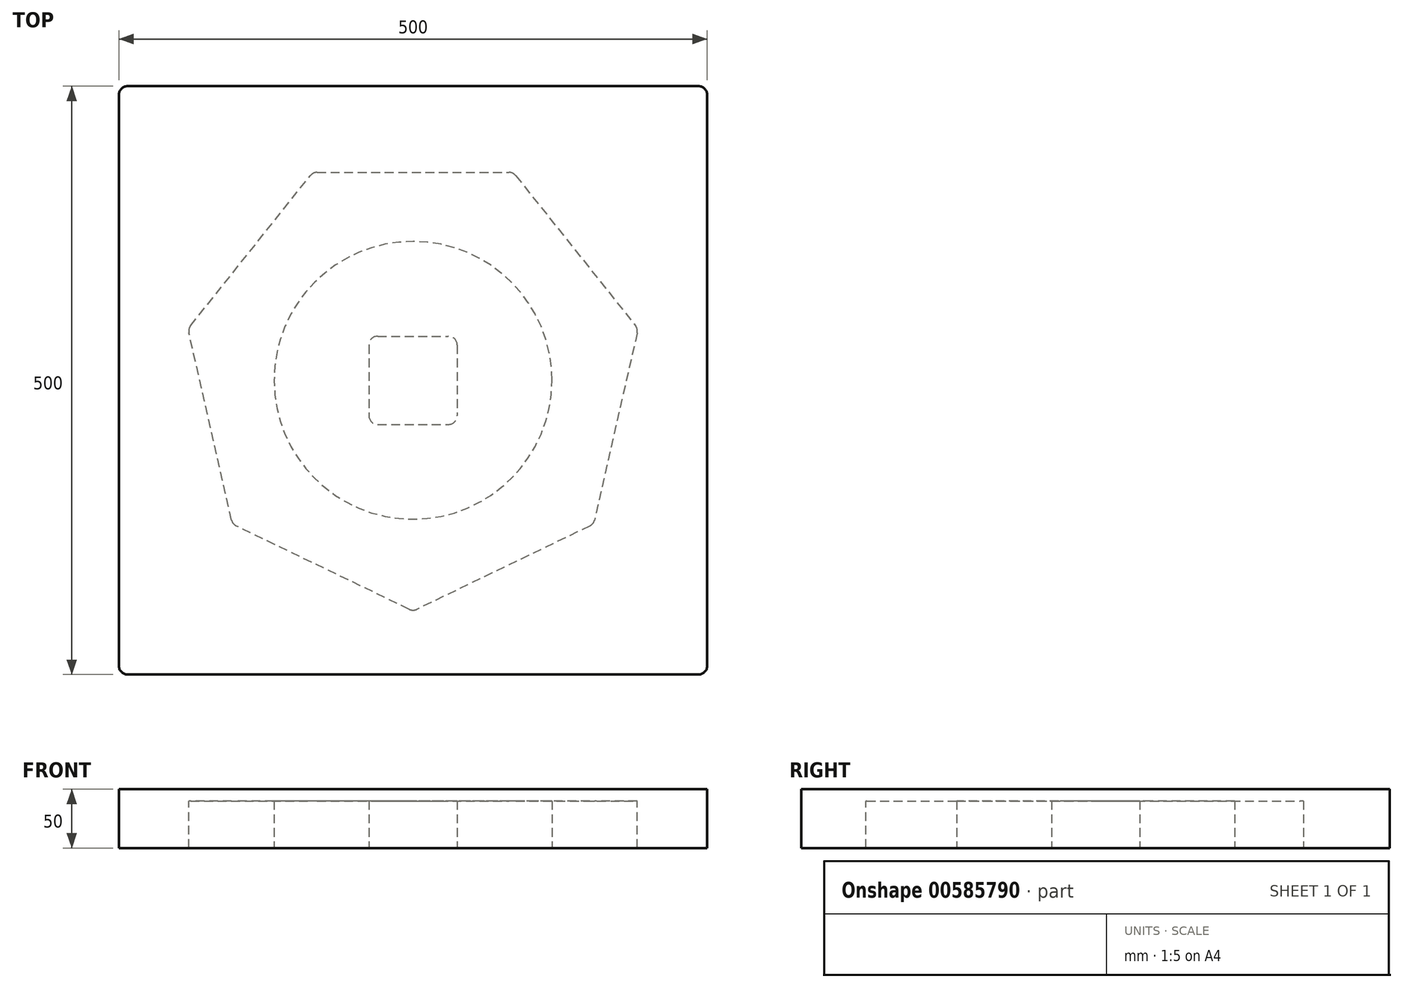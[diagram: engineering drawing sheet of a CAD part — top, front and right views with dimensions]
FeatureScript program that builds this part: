
annotation { "Feature Type Name" : "Feature", "Feature Type Description" : "" }
export const myFeature = defineFeature(function(context is Context, id is Id, definition is map)
    precondition{}
    {
        {
            var Q0;
            Q0=qCreatedBy(makeId("Top.planeOp"),FACE);
            var sketch = newSketch(context, id + "F0", { "sketchPlane" : qUnion([Q0])});
            skLineSegment(sketch, "E0.bottom", {"start": v(-250, 250) * mm, "end": v(250, 250) * mm});
            skLineSegment(sketch, "E0.top", {"start": v(-250, -250) * mm, "end": v(250, -250) * mm});
            skLineSegment(sketch, "E0.left", {"start": v(-250, 250) * mm, "end": v(-250, -250) * mm});
            skLineSegment(sketch, "E0.right", {"start": v(250, 250) * mm, "end": v(250, -250) * mm});
            skPoint(sketch, "E0.middle", {"position": v(0, 0) * mm});
            skCircle(sketch, "E1.cCircle", {"center": v(0, 0) * mm, "radius": 176.72 * mm, "construction": true});
            skLineSegment(sketch, "E1.0", {"start": v(-85.1, 176.72) * mm, "end": v(85.1, 176.72) * mm});
            skLineSegment(sketch, "E1.1", {"start": v(85.1, 176.72) * mm, "end": v(191.23, 43.65) * mm});
            skLineSegment(sketch, "E1.2", {"start": v(191.23, 43.65) * mm, "end": v(153.36, -122.3) * mm});
            skLineSegment(sketch, "E1.3", {"start": v(153.36, -122.3) * mm, "end": v(0, -196.15) * mm});
            skLineSegment(sketch, "E1.4", {"start": v(0, -196.15) * mm, "end": v(-153.36, -122.3) * mm});
            skLineSegment(sketch, "E1.5", {"start": v(-153.36, -122.3) * mm, "end": v(-191.23, 43.65) * mm});
            skLineSegment(sketch, "E1.6", {"start": v(-191.23, 43.65) * mm, "end": v(-85.1, 176.72) * mm});
            skPoint(sketch, "E1.0.midPoint", {"position": v(0, 176.72) * mm});
            skCircle(sketch, "E2", {"center": v(0, 0) * mm, "radius": 118.02 * mm});
            skLineSegment(sketch, "E3.bottom", {"start": v(-37.5, 37.5) * mm, "end": v(37.5, 37.5) * mm});
            skLineSegment(sketch, "E3.top", {"start": v(-37.5, -37.5) * mm, "end": v(37.5, -37.5) * mm});
            skLineSegment(sketch, "E3.left", {"start": v(-37.5, 37.5) * mm, "end": v(-37.5, -37.5) * mm});
            skLineSegment(sketch, "E3.right", {"start": v(37.5, 37.5) * mm, "end": v(37.5, -37.5) * mm});
            skSolve(sketch);
        }
        {
            var Q0;
            Q0=makeQuery(id+"F0.imprint","IMPRINT",FACE,{"disambiguationData":[TD([[makeQuery(id+"F0.imprint","IMPRINT",EDGE,{"derivedFrom":sQuery(id+"F0.wireOp",EDGE,"E0.bottom")}),-1.0]])]});
            var Q1;
            Q1=makeQuery(id+"F0.imprint","IMPRINT",FACE,{"disambiguationData":[TD([[makeQuery(id+"F0.imprint","IMPRINT",EDGE,{"derivedFrom":sQuery(id+"F0.wireOp",EDGE,"E2")}),1.0]])]});
            var Q2;
            Q2=makeQuery(id+"F0.imprint","IMPRINT",FACE,{"disambiguationData":[TD([[makeQuery(id+"F0.imprint","IMPRINT",EDGE,{"derivedFrom":sQuery(id+"F0.wireOp",EDGE,"E1.0")}),-1.0]])]});
            var Q3;
            Q3=makeQuery(id+"F0.imprint","IMPRINT",FACE,{"disambiguationData":[TD([[makeQuery(id+"F0.imprint","IMPRINT",EDGE,{"derivedFrom":sQuery(id+"F0.wireOp",EDGE,"E3.bottom")}),-1.0]])]});
            extrude(context, id + "F1", {"entities" : qUnion([Q0, Q1, Q2, Q3]), "depth" : 50 * mm, "offsetDistance" : 25 * mm});
        }
        {
            var Q0;
            Q0=makeQuery(id+"F0.imprint","IMPRINT",FACE,{"disambiguationData":[TD([[makeQuery(id+"F0.imprint","IMPRINT",EDGE,{"derivedFrom":sQuery(id+"F0.wireOp",EDGE,"E1.0")}),-1.0]])]});
            var Q1;
            Q1=makeQuery(id+"F0.imprint","IMPRINT",FACE,{"disambiguationData":[TD([[makeQuery(id+"F0.imprint","IMPRINT",EDGE,{"derivedFrom":sQuery(id+"F0.wireOp",EDGE,"E3.bottom")}),-1.0]])]});
            extrude(context, id + "F2", {"entities" : qUnion([Q0, Q1]), "operationType" : NewBodyOperationType.REMOVE, "depth" : 40 * mm, "offsetDistance" : 25 * mm});
        }
        {
            var Q0;
            Q0=makeQuery(id+"F1.opExtrude","SWEPT_EDGE",EDGE,{"disambiguationData":[OSD([sQuery(id+"F0.wireOp",EDGE,"E0.top"),sQuery(id+"F0.wireOp",EDGE,"E0.right")])]});
            var Q1;
            Q1=makeQuery(id+"F1.opExtrude","SWEPT_EDGE",EDGE,{"disambiguationData":[OSD([sQuery(id+"F0.wireOp",EDGE,"E0.top"),sQuery(id+"F0.wireOp",EDGE,"E0.left")])]});
            var Q2;
            Q2=makeQuery(id+"F1.opExtrude","SWEPT_EDGE",EDGE,{"disambiguationData":[OSD([sQuery(id+"F0.wireOp",EDGE,"E0.bottom"),sQuery(id+"F0.wireOp",EDGE,"E0.left")])]});
            var Q3;
            Q3=makeQuery(id+"F1.opExtrude","SWEPT_EDGE",EDGE,{"disambiguationData":[OSD([sQuery(id+"F0.wireOp",EDGE,"E0.bottom"),sQuery(id+"F0.wireOp",EDGE,"E0.right")])]});
            var Q4;
            Q4=makeQuery(id+"F2.boolean.opBoolean","COPY",EDGE,{"derivedFrom":makeQuery(id+"F2.opExtrude","SWEPT_EDGE",EDGE,{"disambiguationData":[OSD([sQuery(id+"F0.wireOp",EDGE,"E1.3"),sQuery(id+"F0.wireOp",EDGE,"E1.4")])]})});
            var Q5;
            Q5=makeQuery(id+"F2.boolean.opBoolean","COPY",EDGE,{"derivedFrom":makeQuery(id+"F2.opExtrude","SWEPT_EDGE",EDGE,{"disambiguationData":[OSD([sQuery(id+"F0.wireOp",EDGE,"E1.4"),sQuery(id+"F0.wireOp",EDGE,"E1.5")])]})});
            var Q6;
            Q6=makeQuery(id+"F2.boolean.opBoolean","COPY",EDGE,{"derivedFrom":makeQuery(id+"F2.opExtrude","SWEPT_EDGE",EDGE,{"disambiguationData":[OSD([sQuery(id+"F0.wireOp",EDGE,"E1.2"),sQuery(id+"F0.wireOp",EDGE,"E1.3")])]})});
            var Q7;
            Q7=makeQuery(id+"F2.boolean.opBoolean","COPY",EDGE,{"derivedFrom":makeQuery(id+"F2.opExtrude","SWEPT_EDGE",EDGE,{"disambiguationData":[OSD([sQuery(id+"F0.wireOp",EDGE,"E1.1"),sQuery(id+"F0.wireOp",EDGE,"E1.2")])]})});
            var Q8;
            Q8=makeQuery(id+"F2.boolean.opBoolean","COPY",EDGE,{"derivedFrom":makeQuery(id+"F2.opExtrude","SWEPT_EDGE",EDGE,{"disambiguationData":[OSD([sQuery(id+"F0.wireOp",EDGE,"E1.0"),sQuery(id+"F0.wireOp",EDGE,"E1.1")])]})});
            var Q9;
            Q9=makeQuery(id+"F2.boolean.opBoolean","COPY",EDGE,{"derivedFrom":makeQuery(id+"F2.opExtrude","SWEPT_EDGE",EDGE,{"disambiguationData":[OSD([sQuery(id+"F0.wireOp",EDGE,"E1.0"),sQuery(id+"F0.wireOp",EDGE,"E1.6")])]})});
            var Q10;
            Q10=makeQuery(id+"F2.boolean.opBoolean","COPY",EDGE,{"derivedFrom":makeQuery(id+"F2.opExtrude","SWEPT_EDGE",EDGE,{"disambiguationData":[OSD([sQuery(id+"F0.wireOp",EDGE,"E1.5"),sQuery(id+"F0.wireOp",EDGE,"E1.6")])]})});
            var Q11;
            Q11=makeQuery(id+"F2.boolean.opBoolean","COPY",EDGE,{"derivedFrom":makeQuery(id+"F2.opExtrude","SWEPT_EDGE",EDGE,{"disambiguationData":[OSD([sQuery(id+"F0.wireOp",EDGE,"E3.top"),sQuery(id+"F0.wireOp",EDGE,"E3.left")])]})});
            var Q12;
            Q12=makeQuery(id+"F2.boolean.opBoolean","COPY",EDGE,{"derivedFrom":makeQuery(id+"F2.opExtrude","SWEPT_EDGE",EDGE,{"disambiguationData":[OSD([sQuery(id+"F0.wireOp",EDGE,"E3.top"),sQuery(id+"F0.wireOp",EDGE,"E3.right")])]})});
            var Q13;
            Q13=makeQuery(id+"F2.boolean.opBoolean","COPY",EDGE,{"derivedFrom":makeQuery(id+"F2.opExtrude","SWEPT_EDGE",EDGE,{"disambiguationData":[OSD([sQuery(id+"F0.wireOp",EDGE,"E3.bottom"),sQuery(id+"F0.wireOp",EDGE,"E3.right")])]})});
            var Q14;
            Q14=makeQuery(id+"F2.boolean.opBoolean","COPY",EDGE,{"derivedFrom":makeQuery(id+"F2.opExtrude","SWEPT_EDGE",EDGE,{"disambiguationData":[OSD([sQuery(id+"F0.wireOp",EDGE,"E3.bottom"),sQuery(id+"F0.wireOp",EDGE,"E3.left")])]})});
            fillet(context, id + "F3", {"entities" : qUnion([Q0, Q1, Q2, Q3, Q4, Q5, Q6, Q7, Q8, Q9, Q10, Q11, Q12, Q13, Q14]), "radius" : 7.5 * mm, "tangentPropagation" : true, "allowEdgeOverflow" : false});
        }
    });
